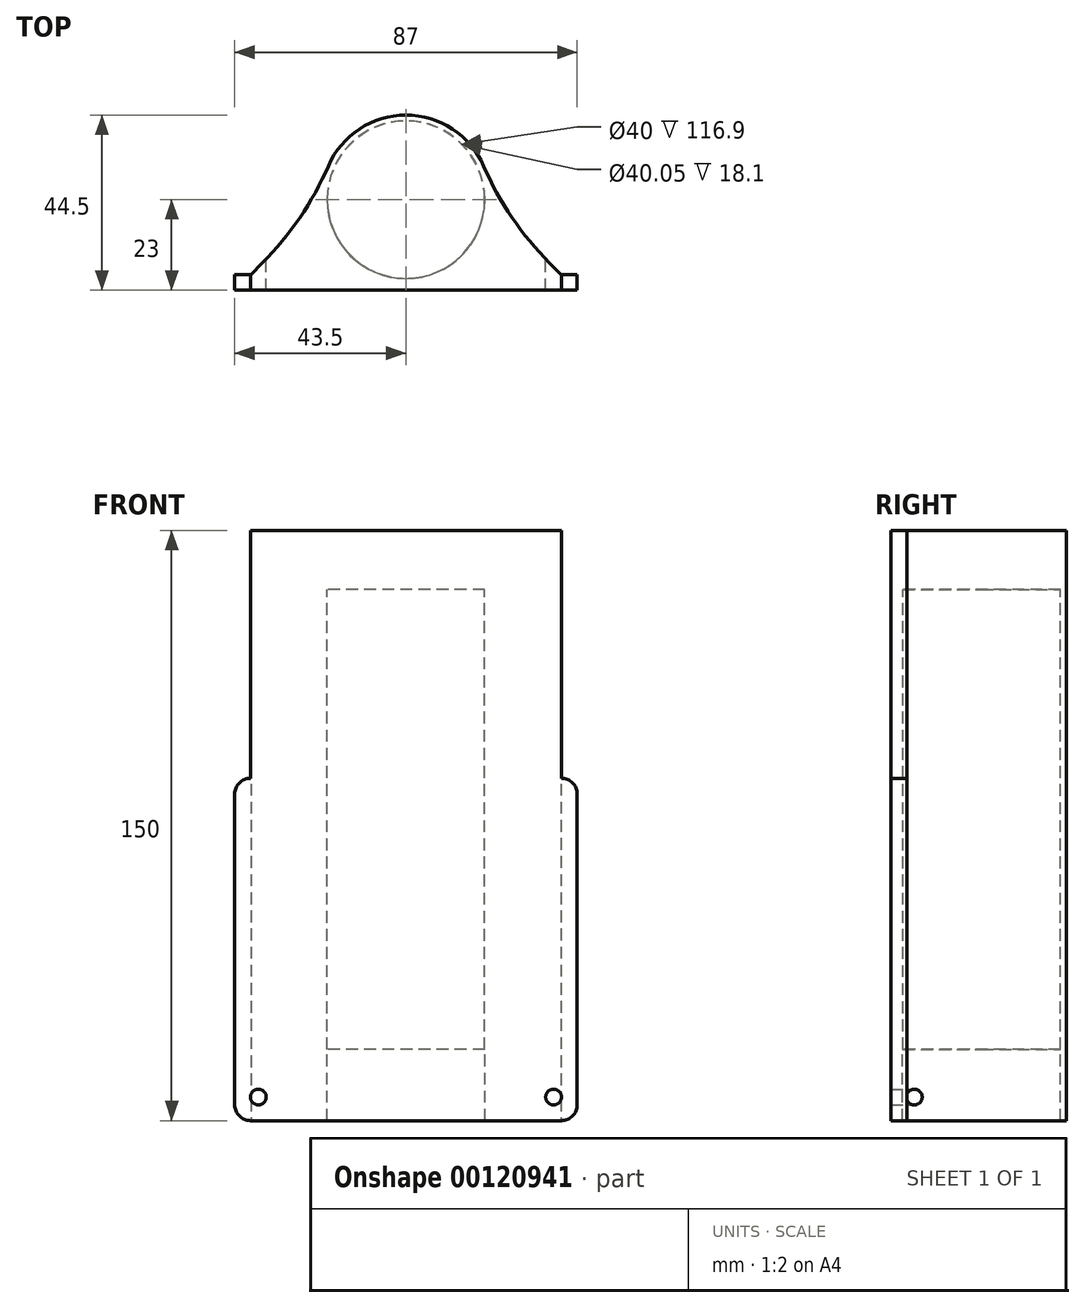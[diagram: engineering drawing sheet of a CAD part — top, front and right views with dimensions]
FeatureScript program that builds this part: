
annotation { "Feature Type Name" : "Feature", "Feature Type Description" : "" }
export const myFeature = defineFeature(function(context is Context, id is Id, definition is map)
    precondition{}
    {
        {
            var Q0;
            Q0=qCreatedBy(makeId("Front.planeOp"),FACE);
            var sketch = newSketch(context, id + "F0", { "sketchPlane" : qUnion([Q0])});
            skLineSegment(sketch, "E0.bottom", {"start": v(-37.5, 37.5) * mm, "end": v(37.5, 37.5) * mm, "construction": true});
            skLineSegment(sketch, "E0.top", {"start": v(-37.5, -37.5) * mm, "end": v(37.5, -37.5) * mm, "construction": true});
            skLineSegment(sketch, "E0.left", {"start": v(-37.5, 37.5) * mm, "end": v(-37.5, -37.5) * mm, "construction": true});
            skLineSegment(sketch, "E0.right", {"start": v(37.5, 37.5) * mm, "end": v(37.5, -37.5) * mm, "construction": true});
            skPoint(sketch, "E0.middle", {"position": v(0, 0) * mm});
            skLineSegment(sketch, "E1.bottom", {"start": v(43.5, -43.5) * mm, "end": v(-43.5, -43.5) * mm});
            skLineSegment(sketch, "E1.top", {"start": v(43.5, 43.5) * mm, "end": v(-43.5, 43.5) * mm});
            skLineSegment(sketch, "E1.left", {"start": v(43.5, -43.5) * mm, "end": v(43.5, 43.5) * mm});
            skLineSegment(sketch, "E1.right", {"start": v(-43.5, -43.5) * mm, "end": v(-43.5, 43.5) * mm});
            skCircle(sketch, "E2", {"center": v(-37.5, 37.5) * mm, "radius": 2 * mm});
            skCircle(sketch, "E3", {"center": v(37.5, 37.5) * mm, "radius": 2 * mm});
            skCircle(sketch, "E4", {"center": v(37.5, -37.5) * mm, "radius": 2 * mm});
            skCircle(sketch, "E5", {"center": v(-37.5, -37.5) * mm, "radius": 2 * mm});
            skSolve(sketch);
        }
        {
            var Q0;
            Q0 = qSketchRegion(id + "F0", true);
            extrude(context, id + "F1", {"entities" : qUnion([Q0]), "depth" : 4 * mm});
        }
        {
            var Q0;
            Q0=makeQuery(id+"F1.opExtrude","SWEPT_EDGE",EDGE,{"disambiguationData":[OSD([sQuery(id+"F0.wireOp",EDGE,"E1.top"),sQuery(id+"F0.wireOp",EDGE,"E1.left")])]});
            var Q1;
            Q1=makeQuery(id+"F1.opExtrude","SWEPT_EDGE",EDGE,{"disambiguationData":[OSD([sQuery(id+"F0.wireOp",EDGE,"E1.top"),sQuery(id+"F0.wireOp",EDGE,"E1.right")])]});
            var Q2;
            Q2=makeQuery(id+"F1.opExtrude","SWEPT_EDGE",EDGE,{"disambiguationData":[OSD([sQuery(id+"F0.wireOp",EDGE,"E1.bottom"),sQuery(id+"F0.wireOp",EDGE,"E1.left")])]});
            var Q3;
            Q3=makeQuery(id+"F1.opExtrude","SWEPT_EDGE",EDGE,{"disambiguationData":[OSD([sQuery(id+"F0.wireOp",EDGE,"E1.bottom"),sQuery(id+"F0.wireOp",EDGE,"E1.right")])]});
            fillet(context, id + "F2", {"entities" : qUnion([Q0, Q1, Q2, Q3]), "radius" : 4 * mm, "tangentPropagation" : true, "allowEdgeOverflow" : false});
        }
        {
            var Q0;
            Q0=makeQuery(id+"F1.opExtrude","CAP_FACE",FACE,{"disambiguationData":[OSD([sQuery(id+"F0.wireOp",EDGE,"E1.bottom"),sQuery(id+"F0.wireOp",EDGE,"E1.top"),sQuery(id+"F0.wireOp",EDGE,"E1.left"),sQuery(id+"F0.wireOp",EDGE,"E1.right"),sQuery(id+"F0.wireOp",EDGE,"E2"),sQuery(id+"F0.wireOp",EDGE,"E3"),sQuery(id+"F0.wireOp",EDGE,"E4"),sQuery(id+"F0.wireOp",EDGE,"E5")])],"isStart":false});
            var sketch = newSketch(context, id + "F3", { "sketchPlane" : qUnion([Q0])});
            skLineSegment(sketch, "E6", {"start": v(-20, 43.5) * mm, "end": v(-20, -43.5) * mm});
            skLineSegment(sketch, "E7", {"start": v(-20, -43.5) * mm, "end": v(20, -43.5) * mm, "construction": true});
            skLineSegment(sketch, "E8", {"start": v(20, -43.5) * mm, "end": v(20, 43.5) * mm});
            skLineSegment(sketch, "E9", {"start": v(20, 43.5) * mm, "end": v(-20, 43.5) * mm, "construction": true});
            skPoint(sketch, "E10", {"position": v(0, -43.5) * mm});
            skPoint(sketch, "E11", {"position": v(-20, 0) * mm});
            skSolve(sketch);
        }
        {
            var Q0;
            Q0=qCreatedBy(makeId("Top.planeOp"),FACE);
            var sketch = newSketch(context, id + "F4", { "sketchPlane" : qUnion([Q0])});
            skLineSegment(sketch, "E12", {"start": v(-19, 19) * mm, "end": v(-19, -1) * mm, "construction": true});
            skLineSegment(sketch, "E13", {"start": v(-19, -1) * mm, "end": v(19, -1) * mm, "construction": true});
            skLineSegment(sketch, "E14", {"start": v(19, -1) * mm, "end": v(19, 19) * mm, "construction": true});
            skPoint(sketch, "E15", {"position": v(-19, 9) * mm});
            skPoint(sketch, "E16", {"position": v(19, 9) * mm});
            skLineSegment(sketch, "E17", {"start": v(-19, 19) * mm, "end": v(-38, 0) * mm});
            skLineSegment(sketch, "E18", {"start": v(19, 19) * mm, "end": v(38, 0) * mm});
            skLineSegment(sketch, "E19.0", {"start": v(-20, 19.42) * mm, "end": v(-39.41, 0) * mm});
            skArc(sketch, "E19.1", {"start": v(0, 39) * mm, "mid": v(-14, 33.29) * mm, "end": v(-20, 19.42) * mm});
            skArc(sketch, "E19.2", {"start": v(20, 19.42) * mm, "mid": v(14, 33.29) * mm, "end": v(0, 39) * mm});
            skLineSegment(sketch, "E19.3", {"start": v(20, 19.42) * mm, "end": v(39.41, 0) * mm});
            skLineSegment(sketch, "E20", {"start": v(-39.41, 0) * mm, "end": v(39.41, 0) * mm});
            skCircle(sketch, "E21", {"center": v(0, 19) * mm, "radius": 20.5 * mm, "construction": true});
            skCircle(sketch, "E22.0", {"center": v(0, 19) * mm, "radius": 21.5 * mm});
            skSolve(sketch);
        }
        {
            var Q0;
            Q0 = qSketchRegion(id + "F4", true);
            extrude(context, id + "F5", {"entities" : qUnion([Q0]), "operationType" : NewBodyOperationType.ADD, "endBound" : BoundingType.SYMMETRIC, "depth" : 87 * mm});
        }
        {
            var Q0;
            Q0=makeQuery(id+"F5.opExtrude","SWEPT_EDGE",EDGE,{"disambiguationData":[OSD([sQuery(id+"F4.wireOp",EDGE,"E19.0"),sQuery(id+"F4.wireOp",EDGE,"E22.0")])]});
            var Q1;
            Q1=makeQuery(id+"F5.opExtrude","SWEPT_EDGE",EDGE,{"disambiguationData":[OSD([sQuery(id+"F4.wireOp",EDGE,"E19.3"),sQuery(id+"F4.wireOp",EDGE,"E22.0")])]});
            fillet(context, id + "F6", {"entities" : qUnion([Q0, Q1]), "radius" : 80 * mm, "tangentPropagation" : true, "allowEdgeOverflow" : false});
        }
        {
            var Q0;
            Q0=makeQuery(id+"F5.boolean.opBoolean","MERGE",FACE,{"derivedFrom":[makeQuery(id+"F1.opExtrude","SWEPT_FACE",FACE,{"disambiguationData":[OSD([sQuery(id+"F0.wireOp",EDGE,"E1.top")])]}),makeQuery(id+"F5.opExtrude","CAP_FACE",FACE,{"disambiguationData":[OSD([sQuery(id+"F4.wireOp",EDGE,"E19.0"),sQuery(id+"F4.wireOp",EDGE,"E19.3"),sQuery(id+"F4.wireOp",EDGE,"E20"),sQuery(id+"F4.wireOp",EDGE,"E22.0")])],"isStart":false})]});
            var sketch = newSketch(context, id + "F7", { "sketchPlane" : qUnion([Q0])});
            skCircle(sketch, "E23", {"center": v(0, 19) * mm, "radius": 20.02 * mm});
            skSolve(sketch);
        }
        {
            var Q0;
            Q0 = qSketchRegion(id + "F7", true);
            extrude(context, id + "F8", {"entities" : qUnion([Q0]), "operationType" : NewBodyOperationType.REMOVE, "endBound" : BoundingType.THROUGH_ALL, "oppositeDirection" : true, "depth" : 25.4 * mm});
        }
        {
            var Q0;
            Q0=qCreatedBy(makeId("Front.planeOp"),FACE);
            var sketch = newSketch(context, id + "F9", { "sketchPlane" : qUnion([Q0])});
            skLineSegment(sketch, "E24.bottom", {"start": v(-37.5, 37.5) * mm, "end": v(37.5, 37.5) * mm});
            skLineSegment(sketch, "E24.top", {"start": v(-37.5, -37.5) * mm, "end": v(37.5, -37.5) * mm, "construction": true});
            skLineSegment(sketch, "E24.left", {"start": v(-37.5, 37.5) * mm, "end": v(-37.5, -37.5) * mm});
            skLineSegment(sketch, "E24.right", {"start": v(37.5, 37.5) * mm, "end": v(37.5, -37.5) * mm, "construction": true});
            skCircle(sketch, "E25", {"center": v(-37.5, 37.5) * mm, "radius": 2 * mm});
            skCircle(sketch, "E26.0.1.0", {"center": v(-37.5, -37.5) * mm, "radius": 2 * mm});
            skCircle(sketch, "E26.1.0.0", {"center": v(37.5, 37.5) * mm, "radius": 2 * mm});
            skCircle(sketch, "E26.1.1.0", {"center": v(37.5, -37.5) * mm, "radius": 2 * mm});
            skLineSegment(sketch, "E26.direction1", {"start": v(-37.5, 37.5) * mm, "end": v(37.5, 37.5) * mm, "construction": true});
            skLineSegment(sketch, "E26.direction2", {"start": v(-37.5, 37.5) * mm, "end": v(-37.5, -37.5) * mm, "construction": true});
            skSolve(sketch);
        }
        {
            var Q0;
            Q0 = qSketchRegion(id + "F9", true);
            extrude(context, id + "F10", {"entities" : qUnion([Q0]), "operationType" : NewBodyOperationType.REMOVE, "endBound" : BoundingType.THROUGH_ALL, "oppositeDirection" : true, "depth" : 25.4 * mm});
        }
        {
            var Q0;
            Q0=makeQuery(id+"F5.boolean.opBoolean","MERGE",FACE,{"derivedFrom":[makeQuery(id+"F1.opExtrude","SWEPT_FACE",FACE,{"disambiguationData":[OSD([sQuery(id+"F0.wireOp",EDGE,"E1.bottom")])]}),makeQuery(id+"F5.opExtrude","CAP_FACE",FACE,{"disambiguationData":[OSD([sQuery(id+"F4.wireOp",EDGE,"E19.0"),sQuery(id+"F4.wireOp",EDGE,"E19.3"),sQuery(id+"F4.wireOp",EDGE,"E20"),sQuery(id+"F4.wireOp",EDGE,"E22.0")])],"isStart":true})]});
            var sketch = newSketch(context, id + "F11", { "sketchPlane" : qUnion([Q0])});
            skCircle(sketch, "E27", {"center": v(0, -19) * mm, "radius": 20 * mm});
            skSolve(sketch);
        }
        {
            var Q0;
            Q0 = qSketchRegion(id + "F11", true);
            extrude(context, id + "F12", {"entities" : qUnion([Q0]), "oppositeDirection" : true, "depth" : 10 * mm});
        }
        {
            var Q0;
            Q0=makeQuery(id+"F12.opExtrude","SWEPT_BODY",BODY,{"disambiguationData":[OSD([sQuery(id+"F11.wireOp",EDGE,"E27")])]});
            deleteBodies(context, id + "F13", {"entities" : qUnion([Q0])});
        }
        {
            var Q0;
            Q0=qCreatedBy(makeId("Top.planeOp"),FACE);
            var sketch = newSketch(context, id + "F14", { "sketchPlane" : qUnion([Q0])});
            skLineSegment(sketch, "E28.0", {"start": v(39.5, -4) * mm, "end": v(39.5, 0) * mm});
            skLineSegment(sketch, "E28.1", {"start": v(-39.5, -4) * mm, "end": v(39.5, -4) * mm});
            skLineSegment(sketch, "E28.2", {"start": v(39.5, 0) * mm, "end": v(39.41, 0) * mm});
            skLineSegment(sketch, "E28.3", {"start": v(-39.5, 0) * mm, "end": v(-39.5, -4) * mm});
            skLineSegment(sketch, "E28.4", {"start": v(-39.41, 0) * mm, "end": v(-39.5, 0) * mm});
            skLineSegment(sketch, "E28.5", {"start": v(-36.52, 2.9) * mm, "end": v(-39.41, 0) * mm});
            skLineSegment(sketch, "E28.6", {"start": v(39.41, 0) * mm, "end": v(36.52, 2.9) * mm});
            skArc(sketch, "E28.7", {"start": v(36.52, 2.9) * mm, "mid": v(26.96, 14.44) * mm, "end": v(19.72, 27.57) * mm});
            skArc(sketch, "E28.8", {"start": v(19.72, 27.57) * mm, "mid": v(0, 40.5) * mm, "end": v(-19.72, 27.57) * mm});
            skArc(sketch, "E28.9", {"start": v(-19.72, 27.57) * mm, "mid": v(-26.96, 14.44) * mm, "end": v(-36.52, 2.9) * mm});
            skSolve(sketch);
        }
        {
            var Q0;
            Q0 = qSketchRegion(id + "F14", true);
            extrude(context, id + "F15", {"entities" : qUnion([Q0]), "operationType" : NewBodyOperationType.ADD, "depth" : 87 * mm / 2 + 63 * mm, "hasSecondDirection" : true, "secondDirectionOppositeDirection" : true, "secondDirectionDepth" : 25.4 * mm});
        }
        {
            var Q0;
            Q0=makeQuery(id+"F15.opExtrude","CAP_FACE",FACE,{"disambiguationData":[OSD([sQuery(id+"F14.wireOp",EDGE,"E28.0"),sQuery(id+"F14.wireOp",EDGE,"E28.1"),sQuery(id+"F14.wireOp",EDGE,"E28.2"),sQuery(id+"F14.wireOp",EDGE,"E28.3"),sQuery(id+"F14.wireOp",EDGE,"E28.4"),sQuery(id+"F14.wireOp",EDGE,"E28.5"),sQuery(id+"F14.wireOp",EDGE,"E28.6"),sQuery(id+"F14.wireOp",EDGE,"E28.7"),sQuery(id+"F14.wireOp",EDGE,"E28.8"),sQuery(id+"F14.wireOp",EDGE,"E28.9")])],"isStart":false});
            var sketch = newSketch(context, id + "F16", { "sketchPlane" : qUnion([Q0])});
            skCircle(sketch, "E29", {"center": v(0, 19) * mm, "radius": 20 * mm});
            skSolve(sketch);
        }
        {
            var Q0;
            Q0 = qSketchRegion(id + "F16", true);
            extrude(context, id + "F17", {"entities" : qUnion([Q0]), "operationType" : NewBodyOperationType.REMOVE, "endBound" : BoundingType.THROUGH_ALL, "oppositeDirection" : true, "depth" : 25.4 * mm});
        }
        {
            var Q0;
            Q0=makeQuery(id+"F15.opExtrude","CAP_FACE",FACE,{"disambiguationData":[OSD([sQuery(id+"F14.wireOp",EDGE,"E28.0"),sQuery(id+"F14.wireOp",EDGE,"E28.1"),sQuery(id+"F14.wireOp",EDGE,"E28.2"),sQuery(id+"F14.wireOp",EDGE,"E28.3"),sQuery(id+"F14.wireOp",EDGE,"E28.4"),sQuery(id+"F14.wireOp",EDGE,"E28.5"),sQuery(id+"F14.wireOp",EDGE,"E28.6"),sQuery(id+"F14.wireOp",EDGE,"E28.7"),sQuery(id+"F14.wireOp",EDGE,"E28.8"),sQuery(id+"F14.wireOp",EDGE,"E28.9")])],"isStart":false});
            var sketch = newSketch(context, id + "F18", { "sketchPlane" : qUnion([Q0])});
            skCircle(sketch, "E30", {"center": v(0, 19) * mm, "radius": 20 * mm});
            skSolve(sketch);
        }
        {
            var Q0;
            Q0 = qSketchRegion(id + "F18", true);
            extrude(context, id + "F19", {"entities" : qUnion([Q0]), "operationType" : NewBodyOperationType.ADD, "oppositeDirection" : true, "depth" : 15 * mm});
        }
    });
